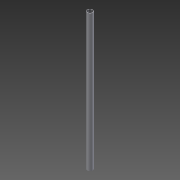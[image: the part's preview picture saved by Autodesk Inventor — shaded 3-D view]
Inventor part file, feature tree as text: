
AUTODESK INVENTOR PART (.ipt)
format: ipt  version: 2015 (Build 190159000, 159)  size: 85,504 bytes
history: native  units: mm
features: thread x2, other x1, extrude x1, shell x1, sketch x1
ambient origin geometry x8: Origin, YZ Plane, XZ Plane, XY Plane, X Axis, Y Axis, Z Axis, Center Point
bodies: Body1 (feature_tree)
feature tree (6):
  other  "Bryła1"
  extrude  "Wyciągnięcie proste1"  Depth=18.0mm
  shell  "Skorupa1"  Thickness=450.0mm
  thread  "Gwint1"
  thread  "Gwint2"
  sketch  "Szkic1"
